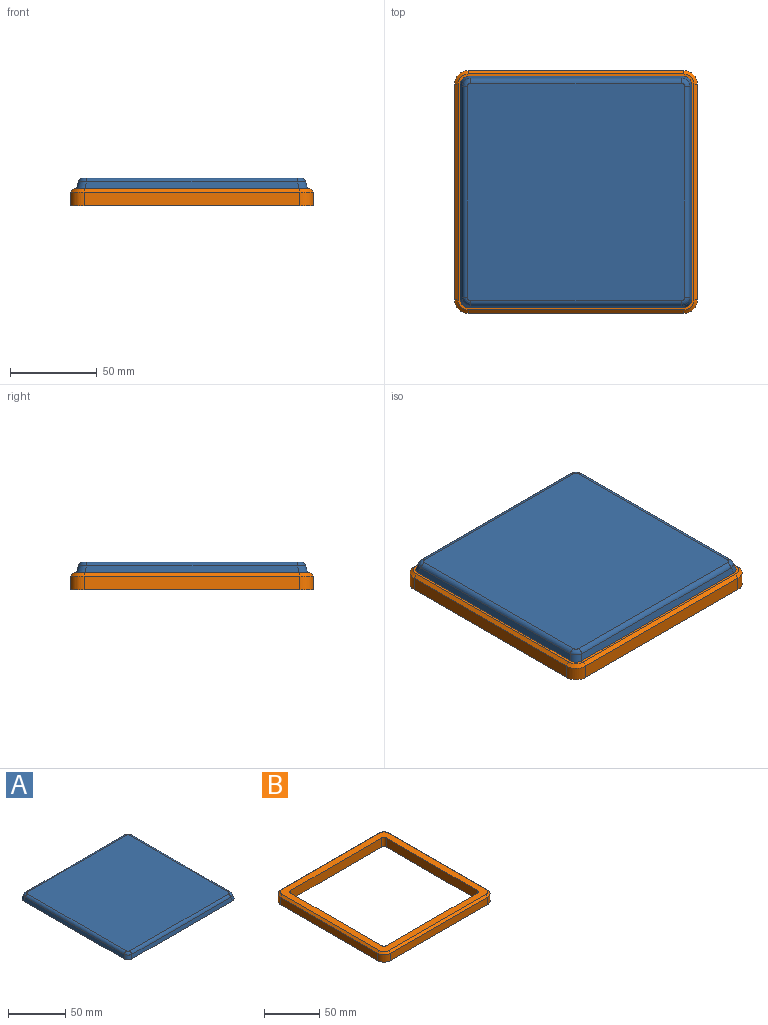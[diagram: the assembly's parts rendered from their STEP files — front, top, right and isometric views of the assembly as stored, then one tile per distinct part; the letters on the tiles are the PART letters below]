
ASSEMBLY  parts=2 mates=1
PART A: 18 faces, bbox 133.5x133.5x6.5 mm
  f0: plane 123.56x3.78mm, normal (0,0.97,0.26), area 479.1mm2, adj f4,f6,f9,f10
  f1: plane 123.56x3.78mm, normal (-0.97,0,0.26), area 479.1mm2, adj f4,f6,f7,f13
  f2: plane 123.56x3.78mm, normal (0,-0.97,0.26), area 479.1mm2, adj f4,f7,f8,f17
  f3: plane 123.56x3.78mm, normal (0.97,0,0.26), area 479.1mm2, adj f4,f8,f9,f14
  f4: plane 133.22x133.22mm, normal (0,0,-1), area 17726.7mm2, adj f0,f1,f2,f3,f6,f7,f8,f9
  f5: plane 125.4x125.4mm, normal (0,0,1), area 15721mm2, adj f10,f11,f12,f13,f14,f15,f16,f17
  f6: cylinder r=5mm len=5.97mm, axis (0.25,-0.25,0.94), area 31.9mm2, adj f0,f1,f4,f11
  f7: cylinder r=5mm len=5.97mm, axis (0.25,0.25,0.94), area 31.9mm2, adj f1,f2,f4,f15
  f8: cylinder r=5mm len=5.97mm, axis (-0.25,0.25,0.94), area 31.9mm2, adj f2,f3,f4,f16
  f9: cylinder r=5mm len=5.97mm, axis (-0.25,-0.25,0.94), area 31.9mm2, adj f0,f3,f4,f12
  f10: cylinder r=3mm len=121.53mm, axis (1,0,0), area 477.3mm2, adj f0,f5,f11,f12
  f11: bspline ~4.83x4.83mm, area 20.9mm2, adj f5,f6,f10,f13
  f12: bspline ~4.83x4.83mm, area 20.9mm2, adj f5,f9,f10,f14
  f13: cylinder r=3mm len=121.53mm, axis (0,-1,0), area 477.3mm2, adj f1,f5,f11,f15
  f14: cylinder r=3mm len=121.53mm, axis (0,-1,0), area 477.3mm2, adj f3,f5,f12,f16
  f15: bspline ~4.83x4.83mm, area 20.9mm2, adj f5,f7,f13,f17
  f16: bspline ~4.83x4.83mm, area 20.9mm2, adj f5,f8,f14,f17
  f17: cylinder r=3mm len=121.53mm, axis (1,0,0), area 477.3mm2, adj f2,f5,f15,f16
PART B: 26 faces, bbox 140x140x10 mm
  f0: plane 124x8mm, normal (0,1,0), area 992mm2, adj f8,f10,f13,f17
  f1: plane 124x8mm, normal (-1,0,0), area 992mm2, adj f8,f10,f11,f14
  f2: plane 124x8mm, normal (0,-1,0), area 992mm2, adj f8,f11,f12,f18
  f3: plane 116x10mm, normal (1,0,0), area 1160mm2, adj f8,f9,f22,f25
  f4: plane 116x10mm, normal (0,-1,0), area 1160mm2, adj f8,f9,f22,f23
  f5: plane 116x10mm, normal (-1,0,0), area 1160mm2, adj f8,f9,f23,f24
  f6: plane 116x10mm, normal (0,1,0), area 1160mm2, adj f8,f9,f24,f25
  f7: plane 124x8mm, normal (1,0,0), area 992mm2, adj f8,f12,f13,f21
  f8: plane 140x140mm, normal (0,0,-1), area 4668.8mm2, adj f0,f1,f2,f3,f4,f5,f6,f7
  f9: plane 136x136mm, normal (0,0,1), area 3588.8mm2, adj f3,f4,f5,f6,f14,f15,f16,f17
  f10: cylinder r=8mm len=8mm, axis (0,0,-1), area 100.5mm2, adj f0,f1,f8,f15
  f11: cylinder r=8mm len=8mm, axis (0,0,1), area 100.5mm2, adj f1,f2,f8,f16
  f12: cylinder r=8mm len=8mm, axis (0,0,-1), area 100.5mm2, adj f2,f7,f8,f20
  f13: cylinder r=8mm len=8mm, axis (0,0,1), area 100.5mm2, adj f0,f7,f8,f19
  f14: plane 124x2mm, normal (-0.71,0,0.71), area 350.7mm2, adj f1,f9,f15,f16
  f15: cone r=6mm half-angle=45deg, axis (0,0,-1), area 31.1mm2, adj f9,f10,f14,f17
  f16: cone r=6mm half-angle=45deg, axis (0,0,-1), area 31.1mm2, adj f9,f11,f14,f18
  f17: plane 124x2mm, normal (0,0.71,0.71), area 350.7mm2, adj f0,f9,f15,f19
  f18: plane 124x2mm, normal (0,-0.71,0.71), area 350.7mm2, adj f2,f9,f16,f20
  f19: cone r=6mm half-angle=45deg, axis (0,0,-1), area 31.1mm2, adj f9,f13,f17,f21
  f20: cone r=6mm half-angle=45deg, axis (0,0,-1), area 31.1mm2, adj f9,f12,f18,f21
  f21: plane 124x2mm, normal (0.71,0,0.71), area 350.7mm2, adj f7,f9,f19,f20
  f22: cylinder r=3mm len=10mm, axis (0,0,1), area 47.1mm2, adj f3,f4,f8,f9
  f23: cylinder r=3mm len=10mm, axis (0,0,-1), area 47.1mm2, adj f4,f5,f8,f9
  f24: cylinder r=3mm len=10mm, axis (0,0,1), area 47.1mm2, adj f5,f6,f8,f9
  f25: cylinder r=3mm len=10mm, axis (0,0,-1), area 47.1mm2, adj f3,f6,f8,f9
PLACE A t=(25.73,179.23,65.4)mm
PLACE B t=(25.73,179.23,59.4)mm
MATE parallel A.f4 <-> B.f9  axis (0,0,-1) through (25.73,179.23,59.4)mm
